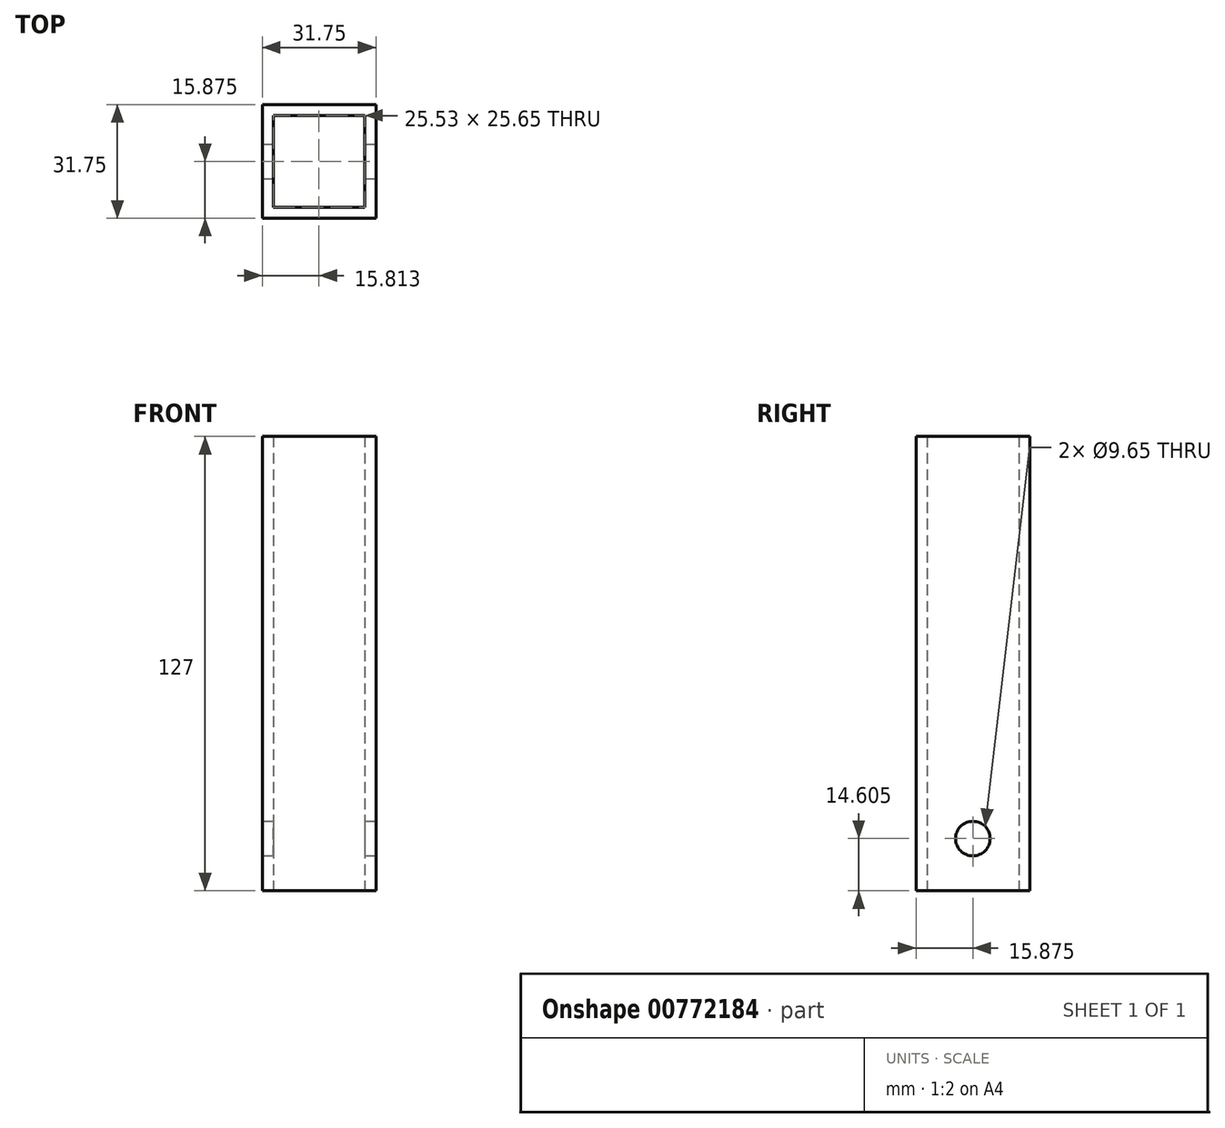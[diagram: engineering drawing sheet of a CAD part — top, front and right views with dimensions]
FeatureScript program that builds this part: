
annotation { "Feature Type Name" : "Feature", "Feature Type Description" : "" }
export const myFeature = defineFeature(function(context is Context, id is Id, definition is map)
    precondition{}
    {
        {
            var Q0;
            Q0=qCreatedBy(makeId("Top.planeOp"),FACE);
            var sketch = newSketch(context, id + "F0", { "sketchPlane" : qUnion([Q0])});
            skLineSegment(sketch, "E0.bottom", {"start": v(2.7, 0) * mm, "end": v(34.45, 0) * mm});
            skLineSegment(sketch, "E0.top", {"start": v(2.7, 31.75) * mm, "end": v(34.45, 31.75) * mm});
            skLineSegment(sketch, "E0.left", {"start": v(2.7, 0) * mm, "end": v(2.7, 31.75) * mm});
            skLineSegment(sketch, "E0.right", {"start": v(34.45, 0) * mm, "end": v(34.45, 31.75) * mm});
            skLineSegment(sketch, "E1.bottom", {"start": v(5.75, 3.05) * mm, "end": v(31.28, 3.05) * mm});
            skLineSegment(sketch, "E1.top", {"start": v(5.75, 28.7) * mm, "end": v(31.28, 28.7) * mm});
            skLineSegment(sketch, "E1.left", {"start": v(5.75, 3.05) * mm, "end": v(5.75, 28.7) * mm});
            skLineSegment(sketch, "E1.right", {"start": v(31.28, 3.05) * mm, "end": v(31.28, 28.7) * mm});
            skSolve(sketch);
        }
        {
            var Q0;
            Q0=makeQuery(id+"F0.imprint","IMPRINT",FACE,{"disambiguationData":[TD([[makeQuery(id+"F0.imprint","IMPRINT",EDGE,{"derivedFrom":sQuery(id+"F0.wireOp",EDGE,"E0.bottom")}),1.0]])]});
            extrude(context, id + "F1", {"entities" : qUnion([Q0]), "depth" : 127 * mm, "offsetDistance" : 25.4 * mm});
        }
        {
            var Q0;
            Q0=makeQuery(id+"F1.opExtrude","SWEPT_FACE",FACE,{"disambiguationData":[OSD([sQuery(id+"F0.wireOp",EDGE,"E0.right")])]});
            var sketch = newSketch(context, id + "F2", { "sketchPlane" : qUnion([Q0])});
            skCircle(sketch, "E2", {"center": v(15.87, 14.6) * mm, "radius": 4.83 * mm});
            skLineSegment(sketch, "E3", {"start": v(0, 63.5) * mm, "end": v(31.75, 63.5) * mm, "construction": true});
            skSolve(sketch);
        }
        {
            var Q0;
            Q0=makeQuery(id+"F2.imprint","IMPRINT",FACE,{"disambiguationData":[TD([[makeQuery(id+"F2.imprint","IMPRINT",EDGE,{"derivedFrom":sQuery(id+"F2.wireOp",EDGE,"E2")}),1.0]])]});
            extrude(context, id + "F3", {"entities" : qUnion([Q0]), "operationType" : NewBodyOperationType.REMOVE, "endBound" : BoundingType.THROUGH_ALL, "oppositeDirection" : true, "depth" : 25.4 * mm, "offsetDistance" : 25.4 * mm});
        }
    });
